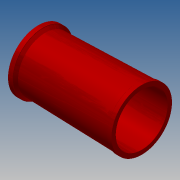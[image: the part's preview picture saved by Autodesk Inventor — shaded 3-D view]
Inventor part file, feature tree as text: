
AUTODESK INVENTOR PART (.ipt)
format: ipt  version: 2017.3 (Build 213257000, 257)  size: 164,864 bytes
history: native  units: in
note: dims shown in document units (in); Inventor stores cm internally (conversion verified against a paired STEP export)
features: other x3, extrude x2, sketch x2, chamfer x1
ambient origin geometry x8: Origin, YZ Plane, XZ Plane, XY Plane, X Axis, Y Axis, Z Axis, Center Point
bodies: Solid1 (feature_tree)
feature tree (8):
  other  "A1-19027-200-04 HCWi reducer.ipt"
  extrude  "Extrusion1"  Depth=0.5in TaperAngle=0.0deg
  extrude  "Extrusion2"  Depth=2.0in
  chamfer  "Chamfer1"  Distance=0.25in Angle=45.0deg
  other  "Solid1::A1-19027-200-04 HCWi reducer.ipt"
  other  "TaggingFeature1"
  sketch  "Sketch2"  dims[d0=0.3937in d1=0.5in d2=2.0in d3=0.0in d4=0.0in]
  sketch  "Sketch3"  dims[d5=0.5in d6=2.0in d7=0.0in d8=0.0in d9=0.25in d10=0.25in d11=0.125in d12=45.0deg d13=0.25in]
